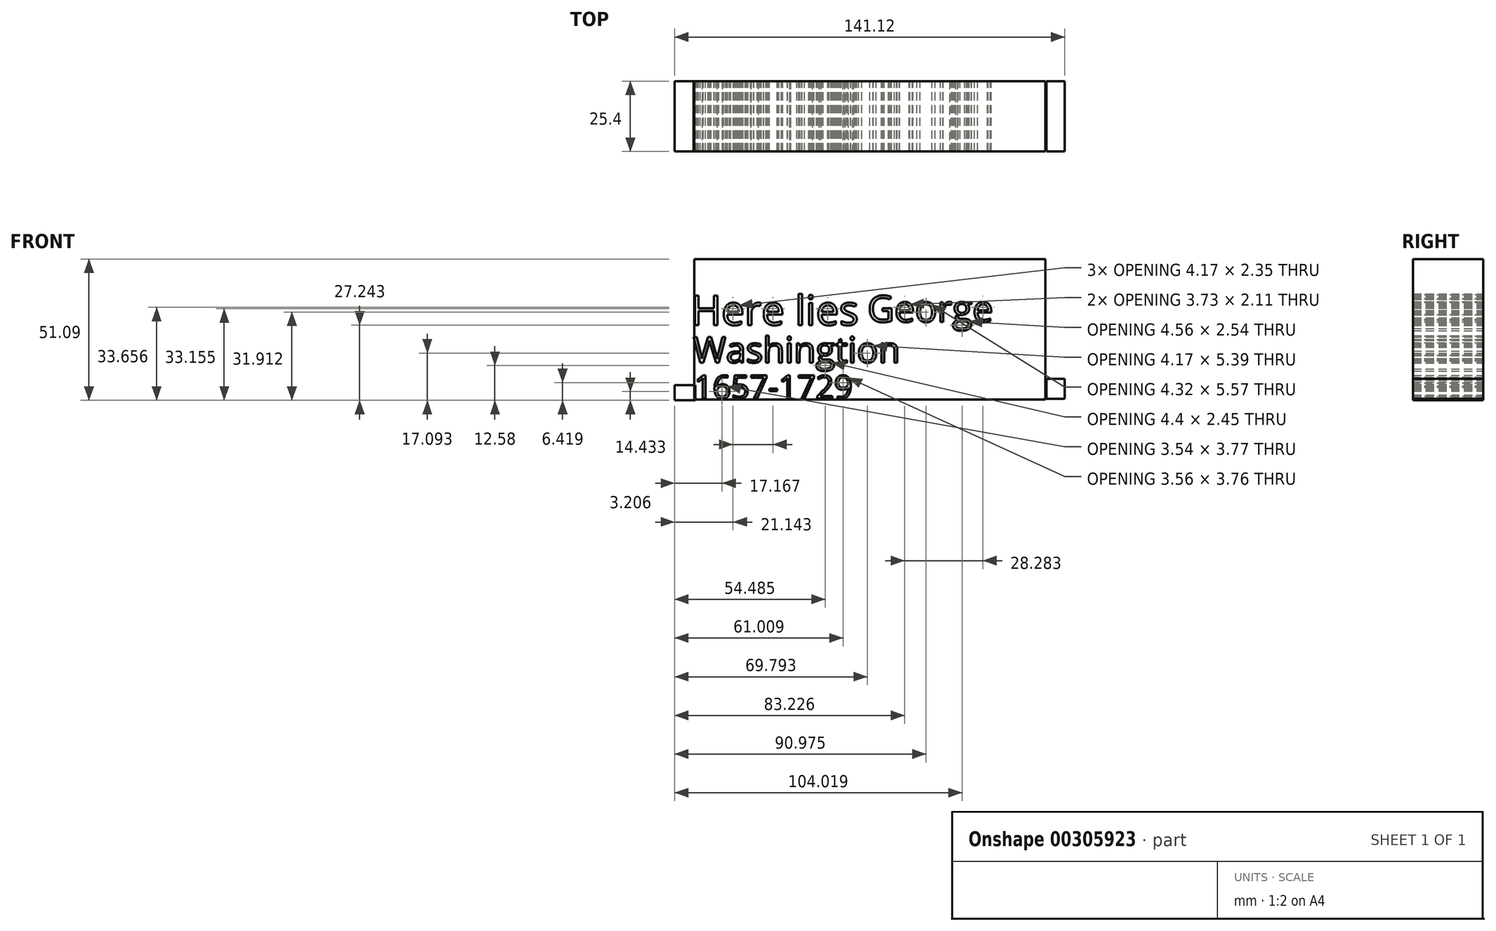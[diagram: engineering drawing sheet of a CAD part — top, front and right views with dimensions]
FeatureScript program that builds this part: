
annotation { "Feature Type Name" : "Feature", "Feature Type Description" : "" }
export const myFeature = defineFeature(function(context is Context, id is Id, definition is map)
    precondition{}
    {
        {
            var Q0;
            Q0=qCreatedBy(makeId("Front.planeOp"),FACE);
            var sketch = newSketch(context, id + "F0", { "sketchPlane" : qUnion([Q0])});
            skLineSegment(sketch, "E0.bottom", {"start": v(-62.68, 13.14) * mm, "end": v(64.32, 13.14) * mm});
            skLineSegment(sketch, "E0.top", {"start": v(-62.68, -37.66) * mm, "end": v(64.32, -37.66) * mm});
            skLineSegment(sketch, "E0.left", {"start": v(-62.68, 13.14) * mm, "end": v(-62.68, -37.66) * mm});
            skLineSegment(sketch, "E0.right", {"start": v(64.32, 13.14) * mm, "end": v(64.32, -37.66) * mm});
            skLineSegment(sketch, "E1.bottom", {"start": v(-39.65, 13.14) * mm, "end": v(36.39, 13.14) * mm});
            skArc(sketch, "E2", {"start": v(36.39, 13.14) * mm, "mid": v(-1.63, 48.7) * mm, "end": v(-39.65, 13.14) * mm});
            skSolve(sketch);
        }
        {
            var Q0;
            Q0=qCreatedBy(makeId("Front.planeOp"),FACE);
            var sketch = newSketch(context, id + "F1", { "sketchPlane" : qUnion([Q0])});
            skLineSegment(sketch, "E3.bottom", {"start": v(64.7, -37.4) * mm, "end": v(71.36, -37.4) * mm});
            skLineSegment(sketch, "E3.top", {"start": v(64.7, -30.15) * mm, "end": v(71.36, -30.15) * mm});
            skLineSegment(sketch, "E3.left", {"start": v(64.7, -37.4) * mm, "end": v(64.7, -30.15) * mm});
            skLineSegment(sketch, "E3.right", {"start": v(71.36, -37.4) * mm, "end": v(71.36, -30.15) * mm});
            skLineSegment(sketch, "E4.bottom", {"start": v(-62.23, -37.95) * mm, "end": v(-69.76, -37.95) * mm});
            skLineSegment(sketch, "E4.top", {"start": v(-62.23, -32.44) * mm, "end": v(-69.76, -32.44) * mm});
            skLineSegment(sketch, "E4.left", {"start": v(-62.23, -37.95) * mm, "end": v(-62.23, -32.44) * mm});
            skLineSegment(sketch, "E4.right", {"start": v(-69.76, -37.95) * mm, "end": v(-69.76, -32.44) * mm});
            skSolve(sketch);
        }
        {
            var Q0;
            Q0=qCreatedBy(makeId("Front.planeOp"),FACE);
            var sketch = newSketch(context, id + "F2", { "sketchPlane" : qUnion([Q0])});
            skText(sketch, "E5", { "text": "Here lies", "fontName": "OpenSans-Regular.ttf"});
            skText(sketch, "E6", { "text": "George", "fontName": "OpenSans-Regular.ttf"});
            skText(sketch, "E7", { "text": "Washingtion", "fontName": "OpenSans-Regular.ttf"});
            skText(sketch, "E8", { "text": "1657-1729", "fontName": "OpenSans-Regular.ttf"});
            const initialGuessF2  = {"E5": [-0.0638, -0.01072, 1, 0, 0.01072], "E6": [0, -0.0096, 1, 0, 0.0096], "E7": [-0.06306, -0.0243, 1, 0, 0.00928], "E8": [-0.0627, -0.03732, 1, 0, 0.00843]};
            skSetInitialGuess(sketch, initialGuessF2);
            skSolve(sketch);
        }
        {
            var Q0;
            Q0=makeQuery(id+"F0.imprint","IMPRINT",FACE,{"disambiguationData":[TD([[makeQuery(id+"F0.imprint","IMPRINT",EDGE,{"derivedFrom":sQuery(id+"F0.wireOp",EDGE,"E0.top")}),1.0]])]});
            var Q1;
            Q1=makeQuery(id+"F1.imprint","IMPRINT",FACE,{"disambiguationData":[TD([[makeQuery(id+"F1.imprint","IMPRINT",EDGE,{"derivedFrom":sQuery(id+"F1.wireOp",EDGE,"E3.bottom")}),1.0]])]});
            var Q2;
            Q2=makeQuery(id+"F1.imprint","IMPRINT",FACE,{"disambiguationData":[TD([[makeQuery(id+"F1.imprint","IMPRINT",EDGE,{"derivedFrom":sQuery(id+"F1.wireOp",EDGE,"E4.bottom")}),-1.0]])]});
            var Q3;
            Q3=makeQuery(id+"F0.imprint","IMPRINT",FACE,{"disambiguationData":[TD([[makeQuery(id+"F0.imprint","IMPRINT",EDGE,{"derivedFrom":sQuery(id+"F0.wireOp",EDGE,"E1.bottom")}),1.0]])]});
            extrude(context, id + "F3", {"entities" : qUnion([Q0, Q1, Q2, Q3]), "depth" : 25.4 * mm});
        }
        {
            var Q0;
            Q0 = qSketchRegion(id + "F2", true);
            extrude(context, id + "F4", {"entities" : qUnion([Q0]), "depth" : 25.4 * mm});
        }
    });
